# Revit family: 50733_UPS250
name_source: partatom
category: Körper
revit_build: Autodesk Revit 2015 (Build: 20140606_1530(x64)
units: mm (PartAtom-declared; Revit-internal decimal feet)

## types (1)
- UnderwaterPower Supply 250 24V/01
    Beschreibung = Power-Measure-control-regulate
    Cable length = 10 m
    Dimensions  LxWxH = 260x162x77 mm
    Effeciency = 90 %
    Environmental condition, dry application = Ambient temperature: max.  30 ° C with natural convection, no direct sun exposure permitted
    Environmental conditions, submersible application = water temperature: min 4 °C to max. 35 °C
    Hersteller = OASE GmbH Post Box 2069, 48469 Hörstel , Germany +49 5454 80-0
    Homepage = http://www.oase-livingwater.com
    Modell = UnderwaterPower Supply 250 24V/01
    Name = UnderwaterPower Supply 250 24V/01
    Nominal input frequency = 50/60 Hz
    Nominal input voltage = 100-240 V/AC
    Protection class = IP 68
    Secondary current = 10.5 A
    Secondary voltage = 24 V/DC
    Slot = 4x 24 V /DC
    Stand by power consumption = 1 %
    Weight = 5.5  kg
    immersion depth max. = 4 m
    oder no. = 50733

## geometry (parser evidence)
native form markers: Blend x6
no freeform markers — native parametric forms only
